FCSTD DOCUMENT  (FreeCAD 0.20R26155 (Git))
Label: 918-418K2022Y40004
License: All rights reserved
LicenseURL: http://en.wikipedia.org/wiki/All_rights_reserved
objects: Sketcher::SketchObject×4, PartDesign::Body×1
note: 5 computed .brp shape members not serialized (recipe doc carries the construction recipe); baked Part::Feature solids carry a one-line shape summary decoded from their .brp

FEATURE [Sketcher::SketchObject] Sketch  label="Edge_Cuts_0.15"
  FullyConstrained = false
  MapMode = 5
  Support = -> [XY_Plane]
  sketch-geometry (8):
    g0: ArcOfCircle CenterX=3.54 CenterY=0 CenterZ=0 NormalX=0 NormalY=0 NormalZ=1 AngleXU=0 Radius=0.29 StartAngle=1.5708 EndAngle=4.71239
    g1: ArcOfCircle CenterX=3.96 CenterY=0 CenterZ=0 NormalX=0 NormalY=0 NormalZ=1 AngleXU=0 Radius=0.29 StartAngle=4.71239 EndAngle=7.85398
    g2: LineSegment StartX=3.54 StartY=-0.29 StartZ=0 EndX=3.96 EndY=-0.29 EndZ=0
    g3: LineSegment StartX=3.96 StartY=0.29 StartZ=0 EndX=3.54 EndY=0.29 EndZ=0
    g4: Circle CenterX=-3.75 CenterY=0 CenterZ=0 NormalX=0 NormalY=0 NormalZ=1 AngleXU=0 Radius=0.33
    g5: LineSegment StartX=3.25 StartY=0.417733 StartZ=0 EndX=3.25 EndY=-0.637407 EndZ=0
    g6: LineSegment StartX=4.25 StartY=0.438122 StartZ=0 EndX=4.25 EndY=-0.525267 EndZ=0
    g7: LineSegment StartX=3.75 StartY=0.282998 StartZ=0 EndX=3.75 EndY=0 EndZ=0
  constraints (18):
    c: Tangent(g0,g2) = -1.5708
    c: Tangent(g2,g1) = -1.5708
    c: Tangent(g1,g3) = -1.5708
    c: Tangent(g3,g0) = -1.5708
    c: Equal(g0,g1)
    c: PointOnObject(g0,g-1)
    c: PointOnObject(g1,g-1)
    c: PointOnObject(g4,g-1)
    c: Radius(g4) = 0.33
    c: DistanceY(g1,g1) = 0.58
    c: Vertical(g5)
    c: Vertical(g6)
    c: Tangent(g6,g1)
    c: Tangent(g5,g0)
    c: Symmetric(g1,g0,g7)
    c: DistanceX(g5,g6) = 1
    c: DistanceX(g4,g7) = 7.5
    c: Symmetric(g4,g7,g-2)
FEATURE [Sketcher::SketchObject] Sketch001  label="Pads_TH_SMD1"
  ExternalGeometry = -> [Sketch]
  FullyConstrained = true
  MapMode = 5
  Support = -> [XY_Plane]
  sketch-geometry (12):
    g0: LineSegment StartX=-2.4 StartY=2.15 StartZ=0 EndX=2.4 EndY=2.15 EndZ=0
    g1: LineSegment StartX=2.4 StartY=2.15 StartZ=0 EndX=2.4 EndY=-2.15 EndZ=0
    g2: LineSegment StartX=2.4 StartY=-2.15 StartZ=0 EndX=-2.4 EndY=-2.15 EndZ=0
    g3: LineSegment StartX=-2.4 StartY=-2.15 StartZ=0 EndX=-2.4 EndY=2.15 EndZ=0
    g4: Circle CenterX=-2.4 CenterY=2.15 CenterZ=0 NormalX=0 NormalY=0 NormalZ=1 AngleXU=0 Radius=0.35
    g5: Circle CenterX=-2.4 CenterY=2.15 CenterZ=0 NormalX=0 NormalY=0 NormalZ=1 AngleXU=0 Radius=0.5
    g6: Circle CenterX=2.4 CenterY=2.15 CenterZ=0 NormalX=0 NormalY=0 NormalZ=1 AngleXU=0 Radius=0.35
    g7: Circle CenterX=2.4 CenterY=2.15 CenterZ=0 NormalX=0 NormalY=0 NormalZ=1 AngleXU=0 Radius=0.5
    g8: Circle CenterX=2.4 CenterY=-2.15 CenterZ=0 NormalX=0 NormalY=0 NormalZ=1 AngleXU=0 Radius=0.5
    g9: Circle CenterX=2.4 CenterY=-2.15 CenterZ=0 NormalX=0 NormalY=0 NormalZ=1 AngleXU=0 Radius=0.35
    g10: Circle CenterX=-2.4 CenterY=-2.15 CenterZ=0 NormalX=0 NormalY=0 NormalZ=1 AngleXU=0 Radius=0.5
    g11: Circle CenterX=-2.4 CenterY=-2.15 CenterZ=0 NormalX=0 NormalY=0 NormalZ=1 AngleXU=0 Radius=0.35
  constraints (27):
    c: Coincident(g0,g1)
    c: Coincident(g1,g2)
    c: Coincident(g2,g3)
    c: Coincident(g3,g0)
    c: Horizontal(g0)
    c: Horizontal(g2)
    c: Vertical(g3)
    c: Symmetric(g0,g1,g-1)
    c: DistanceY(g3,g3) = 4.3
    c: DistanceX(g-3,g2) = 1.35
    c: DistanceX(g-3,g1) = 6.15
    c: Coincident(g4,g0)
    c: Coincident(g5,g4)
    c: Coincident(g6,g0)
    c: Coincident(g7,g6)
    c: Coincident(g8,g1)
    c: Coincident(g9,g8)
    c: Coincident(g10,g2)
    c: Coincident(g11,g10)
    c: Equal(g9,g11)
    c: Equal(g11,g4)
    c: Equal(g4,g6)
    c: Radius(g9) = 0.35
    c: Equal(g8,g10)
    c: Equal(g10,g5)
    c: Equal(g5,g7)
    c: Radius(g8) = 0.5
FEATURE [Sketcher::SketchObject] Sketch002  label="Pads_TH_SMD"
  ExternalGeometry = -> [Sketch]
  FullyConstrained = true
  MapMode = 5
  Support = -> [XY_Plane]
  sketch-geometry (105):
    g0: LineSegment StartX=-2.9 StartY=1.25 StartZ=0 EndX=-2.6 EndY=1.25 EndZ=0
    g1: LineSegment StartX=-2.6 StartY=1.25 StartZ=0 EndX=-2.6 EndY=0.33 EndZ=0
    g2: LineSegment StartX=-2.6 StartY=0.33 StartZ=0 EndX=-2.9 EndY=0.33 EndZ=0
    g3: LineSegment StartX=-2.9 StartY=0.33 StartZ=0 EndX=-2.9 EndY=1.25 EndZ=0
    g4: LineSegment StartX=-2.9 StartY=0.33 StartZ=0 EndX=-3.75 EndY=0.33 EndZ=0
    g5: LineSegment StartX=-2.75 StartY=1.25 StartZ=0 EndX=-2.75 EndY=0.33 EndZ=0
    g6: LineSegment StartX=-2.9 StartY=-0.33 StartZ=0 EndX=-2.6 EndY=-0.33 EndZ=0
    g7: LineSegment StartX=-2.6 StartY=-0.33 StartZ=0 EndX=-2.6 EndY=-1.25 EndZ=0
    g8: LineSegment StartX=-2.6 StartY=-1.25 StartZ=0 EndX=-2.9 EndY=-1.25 EndZ=0
    g9: LineSegment StartX=-2.9 StartY=-1.25 StartZ=0 EndX=-2.9 EndY=-0.33 EndZ=0
    g10: LineSegment StartX=-2.75 StartY=-0.33 StartZ=0 EndX=-2.75 EndY=-1.25 EndZ=0
    g11: LineSegment StartX=-2.9 StartY=-0.33 StartZ=0 EndX=-3.75 EndY=-0.33 EndZ=0
    g12: LineSegment StartX=-2.75 StartY=1.25 StartZ=0 EndX=2.75 EndY=1.25 EndZ=0
    g13: LineSegment StartX=-2.75 StartY=-1.25 StartZ=0 EndX=2.75 EndY=-1.25 EndZ=0
    g14: LineSegment StartX=2.75 StartY=-1.25 StartZ=0 EndX=2.75 EndY=1.25 EndZ=0
    g15: LineSegment StartX=-2.6 StartY=0.33 StartZ=0 EndX=2.75 EndY=0.33 EndZ=0
    g16: LineSegment StartX=-2.6 StartY=-0.33 StartZ=0 EndX=2.75 EndY=-0.33 EndZ=0
    g17: LineSegment StartX=-2.4 StartY=1.25 StartZ=0 EndX=-2.1 EndY=1.25 EndZ=0
    g18: LineSegment StartX=-2.1 StartY=1.25 StartZ=0 EndX=-2.1 EndY=0.33 EndZ=0
    g19: LineSegment StartX=-2.1 StartY=0.33 StartZ=0 EndX=-2.4 EndY=0.33 EndZ=0
    g20: LineSegment StartX=-2.4 StartY=0.33 StartZ=0 EndX=-2.4 EndY=1.25 EndZ=0
    g21: LineSegment StartX=-1.9 StartY=1.25 StartZ=0 EndX=-1.6 EndY=1.25 EndZ=0
    g22: LineSegment StartX=-1.6 StartY=1.25 StartZ=0 EndX=-1.6 EndY=0.33 EndZ=0
    g23: LineSegment StartX=-1.6 StartY=0.33 StartZ=0 EndX=-1.9 EndY=0.33 EndZ=0
    g24: LineSegment StartX=-1.9 StartY=0.33 StartZ=0 EndX=-1.9 EndY=1.25 EndZ=0
    g25: LineSegment StartX=-1.4 StartY=1.25 StartZ=0 EndX=-1.1 EndY=1.25 EndZ=0
    g26: LineSegment StartX=-1.1 StartY=1.25 StartZ=0 EndX=-1.1 EndY=0.33 EndZ=0
    g27: LineSegment StartX=-1.1 StartY=0.33 StartZ=0 EndX=-1.4 EndY=0.33 EndZ=0
    g28: LineSegment StartX=-1.4 StartY=0.33 StartZ=0 EndX=-1.4 EndY=1.25 EndZ=0
    g29: LineSegment StartX=-0.9 StartY=1.25 StartZ=0 EndX=-0.6 EndY=1.25 EndZ=0
    g30: LineSegment StartX=-0.6 StartY=1.25 StartZ=0 EndX=-0.6 EndY=0.33 EndZ=0
    g31: LineSegment StartX=-0.6 StartY=0.33 StartZ=0 EndX=-0.9 EndY=0.33 EndZ=0
    g32: LineSegment StartX=-0.9 StartY=0.33 StartZ=0 EndX=-0.9 EndY=1.25 EndZ=0
    g33: LineSegment StartX=-0.4 StartY=1.25 StartZ=0 EndX=-0.1 EndY=1.25 EndZ=0
    g34: LineSegment StartX=-0.1 StartY=1.25 StartZ=0 EndX=-0.1 EndY=0.33 EndZ=0
    g35: LineSegment StartX=-0.1 StartY=0.33 StartZ=0 EndX=-0.4 EndY=0.33 EndZ=0
    g36: LineSegment StartX=-0.4 StartY=0.33 StartZ=0 EndX=-0.4 EndY=1.25 EndZ=0
    g37: LineSegment StartX=0.1 StartY=1.25 StartZ=0 EndX=0.4 EndY=1.25 EndZ=0
    g38: LineSegment StartX=0.4 StartY=1.25 StartZ=0 EndX=0.4 EndY=0.33 EndZ=0
    g39: LineSegment StartX=0.4 StartY=0.33 StartZ=0 EndX=0.1 EndY=0.33 EndZ=0
    g40: LineSegment StartX=0.1 StartY=0.33 StartZ=0 EndX=0.1 EndY=1.25 EndZ=0
    g41: LineSegment StartX=0.6 StartY=1.25 StartZ=0 EndX=0.9 EndY=1.25 EndZ=0
    g42: LineSegment StartX=0.9 StartY=1.25 StartZ=0 EndX=0.9 EndY=0.33 EndZ=0
    g43: LineSegment StartX=0.9 StartY=0.33 StartZ=0 EndX=0.6 EndY=0.33 EndZ=0
    g44: LineSegment StartX=0.6 StartY=0.33 StartZ=0 EndX=0.6 EndY=1.25 EndZ=0
    g45: LineSegment StartX=1.1 StartY=1.25 StartZ=0 EndX=1.4 EndY=1.25 EndZ=0
    g46: LineSegment StartX=1.4 StartY=1.25 StartZ=0 EndX=1.4 EndY=0.33 EndZ=0
    g47: LineSegment StartX=1.4 StartY=0.33 StartZ=0 EndX=1.1 EndY=0.33 EndZ=0
    g48: LineSegment StartX=1.1 StartY=0.33 StartZ=0 EndX=1.1 EndY=1.25 EndZ=0
    g49: LineSegment StartX=1.6 StartY=1.25 StartZ=0 EndX=1.9 EndY=1.25 EndZ=0
    g50: LineSegment StartX=1.9 StartY=1.25 StartZ=0 EndX=1.9 EndY=0.33 EndZ=0
    g51: LineSegment StartX=1.9 StartY=0.33 StartZ=0 EndX=1.6 EndY=0.33 EndZ=0
    g52: LineSegment StartX=1.6 StartY=0.33 StartZ=0 EndX=1.6 EndY=1.25 EndZ=0
    g53: LineSegment StartX=2.1 StartY=1.25 StartZ=0 EndX=2.4 EndY=1.25 EndZ=0
    g54: LineSegment StartX=2.4 StartY=1.25 StartZ=0 EndX=2.4 EndY=0.33 EndZ=0
    g55: LineSegment StartX=2.4 StartY=0.33 StartZ=0 EndX=2.1 EndY=0.33 EndZ=0
    g56: LineSegment StartX=2.1 StartY=0.33 StartZ=0 EndX=2.1 EndY=1.25 EndZ=0
    g57: LineSegment StartX=2.6 StartY=1.25 StartZ=0 EndX=2.9 EndY=1.25 EndZ=0
    g58: LineSegment StartX=2.9 StartY=1.25 StartZ=0 EndX=2.9 EndY=0.33 EndZ=0
    g59: LineSegment StartX=2.9 StartY=0.33 StartZ=0 EndX=2.6 EndY=0.33 EndZ=0
    g60: LineSegment StartX=2.6 StartY=0.33 StartZ=0 EndX=2.6 EndY=1.25 EndZ=0
    g61: LineSegment StartX=-2.4 StartY=-0.33 StartZ=0 EndX=-2.1 EndY=-0.33 EndZ=0
    g62: LineSegment StartX=-2.1 StartY=-0.33 StartZ=0 EndX=-2.1 EndY=-1.25 EndZ=0
    g63: LineSegment StartX=-2.1 StartY=-1.25 StartZ=0 EndX=-2.4 EndY=-1.25 EndZ=0
    g64: LineSegment StartX=-2.4 StartY=-1.25 StartZ=0 EndX=-2.4 EndY=-0.33 EndZ=0
    g65: LineSegment StartX=-1.9 StartY=-0.33 StartZ=0 EndX=-1.6 EndY=-0.33 EndZ=0
    g66: LineSegment StartX=-1.6 StartY=-0.33 StartZ=0 EndX=-1.6 EndY=-1.25 EndZ=0
    g67: LineSegment StartX=-1.6 StartY=-1.25 StartZ=0 EndX=-1.9 EndY=-1.25 EndZ=0
    g68: LineSegment StartX=-1.9 StartY=-1.25 StartZ=0 EndX=-1.9 EndY=-0.33 EndZ=0
    g69: LineSegment StartX=-1.4 StartY=-0.33 StartZ=0 EndX=-1.1 EndY=-0.33 EndZ=0
    g70: LineSegment StartX=-1.1 StartY=-0.33 StartZ=0 EndX=-1.1 EndY=-1.25 EndZ=0
    g71: LineSegment StartX=-1.1 StartY=-1.25 StartZ=0 EndX=-1.4 EndY=-1.25 EndZ=0
    g72: LineSegment StartX=-1.4 StartY=-1.25 StartZ=0 EndX=-1.4 EndY=-0.33 EndZ=0
    g73: LineSegment StartX=-0.9 StartY=-0.33 StartZ=0 EndX=-0.6 EndY=-0.33 EndZ=0
    g74: LineSegment StartX=-0.6 StartY=-0.33 StartZ=0 EndX=-0.6 EndY=-1.25 EndZ=0
    g75: LineSegment StartX=-0.6 StartY=-1.25 StartZ=0 EndX=-0.9 EndY=-1.25 EndZ=0
    g76: LineSegment StartX=-0.9 StartY=-1.25 StartZ=0 EndX=-0.9 EndY=-0.33 EndZ=0
    g77: LineSegment StartX=-0.4 StartY=-0.33 StartZ=0 EndX=-0.1 EndY=-0.33 EndZ=0
    g78: LineSegment StartX=-0.1 StartY=-0.33 StartZ=0 EndX=-0.1 EndY=-1.25 EndZ=0
    g79: LineSegment StartX=-0.1 StartY=-1.25 StartZ=0 EndX=-0.4 EndY=-1.25 EndZ=0
    g80: LineSegment StartX=-0.4 StartY=-1.25 StartZ=0 EndX=-0.4 EndY=-0.33 EndZ=0
    g81: LineSegment StartX=0.1 StartY=-0.33 StartZ=0 EndX=0.4 EndY=-0.33 EndZ=0
    g82: LineSegment StartX=0.4 StartY=-0.33 StartZ=0 EndX=0.4 EndY=-1.25 EndZ=0
    g83: LineSegment StartX=0.4 StartY=-1.25 StartZ=0 EndX=0.1 EndY=-1.25 EndZ=0
    g84: LineSegment StartX=0.1 StartY=-1.25 StartZ=0 EndX=0.1 EndY=-0.33 EndZ=0
    g85: LineSegment StartX=0.6 StartY=-0.33 StartZ=0 EndX=0.9 EndY=-0.33 EndZ=0
    g86: LineSegment StartX=0.9 StartY=-0.33 StartZ=0 EndX=0.9 EndY=-1.25 EndZ=0
    g87: LineSegment StartX=0.9 StartY=-1.25 StartZ=0 EndX=0.6 EndY=-1.25 EndZ=0
    g88: LineSegment StartX=0.6 StartY=-1.25 StartZ=0 EndX=0.6 EndY=-0.33 EndZ=0
    g89: LineSegment StartX=1.1 StartY=-0.33 StartZ=0 EndX=1.4 EndY=-0.33 EndZ=0
    g90: LineSegment StartX=1.4 StartY=-0.33 StartZ=0 EndX=1.4 EndY=-1.25 EndZ=0
    g91: LineSegment StartX=1.4 StartY=-1.25 StartZ=0 EndX=1.1 EndY=-1.25 EndZ=0
    g92: LineSegment StartX=1.1 StartY=-1.25 StartZ=0 EndX=1.1 EndY=-0.33 EndZ=0
    g93: LineSegment StartX=1.6 StartY=-0.33 StartZ=0 EndX=1.9 EndY=-0.33 EndZ=0
    g94: LineSegment StartX=1.9 StartY=-0.33 StartZ=0 EndX=1.9 EndY=-1.25 EndZ=0
    g95: LineSegment StartX=1.9 StartY=-1.25 StartZ=0 EndX=1.6 EndY=-1.25 EndZ=0
    g96: LineSegment StartX=1.6 StartY=-1.25 StartZ=0 EndX=1.6 EndY=-0.33 EndZ=0
    g97: LineSegment StartX=2.1 StartY=-0.33 StartZ=0 EndX=2.4 EndY=-0.33 EndZ=0
    g98: LineSegment StartX=2.4 StartY=-0.33 StartZ=0 EndX=2.4 EndY=-1.25 EndZ=0
    g99: LineSegment StartX=2.4 StartY=-1.25 StartZ=0 EndX=2.1 EndY=-1.25 EndZ=0
    g100: LineSegment StartX=2.1 StartY=-1.25 StartZ=0 EndX=2.1 EndY=-0.33 EndZ=0
    g101: LineSegment StartX=2.6 StartY=-1.25 StartZ=0 EndX=2.9 EndY=-1.25 EndZ=0
    g102: LineSegment StartX=2.9 StartY=-1.25 StartZ=0 EndX=2.9 EndY=-0.33 EndZ=0
    g103: LineSegment StartX=2.9 StartY=-0.33 StartZ=0 EndX=2.6 EndY=-0.33 EndZ=0
    g104: LineSegment StartX=2.6 StartY=-0.33 StartZ=0 EndX=2.6 EndY=-1.25 EndZ=0
  constraints (312):
    c: Coincident(g0,g1)
    c: Coincident(g1,g2)
    c: Coincident(g2,g3)
    c: Coincident(g3,g0)
    c: Horizontal(g0)
    c: Horizontal(g2)
    c: Vertical(g1)
    c: Vertical(g3)
    c: DistanceX(g0,g0) = 0.3
    c: Coincident(g4,g2)
    c: Horizontal(g4)
    c: Tangent(g4,g-3) = -1.5708
    c: PointOnObject(g5,g0)
    c: PointOnObject(g5,g2)
    c: Symmetric(g1,g2,g5)
    c: DistanceX(g-3,g5) = 1
    c: DistanceY(g-3,g5) = 1.25
    c: Coincident(g6,g7)
    c: Coincident(g7,g8)
    c: Coincident(g8,g9)
    c: Coincident(g9,g6)
    c: Horizontal(g6)
    c: Horizontal(g8)
    c: Vertical(g7)
    c: Vertical(g9)
    c: DistanceX(g8,g8) = 0.3
    c: PointOnObject(g10,g6)
    c: PointOnObject(g10,g8)
    c: Symmetric(g7,g8,g10)
    c: Coincident(g11,g6)
    c: Horizontal(g11)
    c: Tangent(g11,g-3) = 1.5708
    c: DistanceY(g8,g-3) = 1.25
    c: DistanceX(g-3,g10) = 1
    c: Coincident(g12,g5)
    c: Horizontal(g12)
    c: Coincident(g13,g10)
    c: Horizontal(g13)
    c: Coincident(g14,g13)
    c: Coincident(g14,g12)
    c: Vertical(g14)
    c: DistanceX(g-3,g12) = 6.5
    c: Coincident(g15,g1)
    c: PointOnObject(g15,g14)
    c: Horizontal(g15)
    c: Coincident(g16,g6)
    c: PointOnObject(g16,g14)
    c: Horizontal(g16)
    c: Coincident(g17,g18)
    c: Coincident(g18,g19)
    c: Coincident(g19,g20)
    c: Coincident(g20,g17)
    c: Horizontal(g17)
    c: Horizontal(g19)
    c: Vertical(g18)
    c: Vertical(g20)
    c: PointOnObject(g17,g12)
    c: PointOnObject(g18,g15)
    c: Coincident(g21,g22)
    c: Coincident(g22,g23)
    c: Coincident(g23,g24)
    c: Coincident(g24,g21)
    c: Horizontal(g21)
    c: Horizontal(g23)
    c: Vertical(g22)
    c: Vertical(g24)
    c: PointOnObject(g21,g12)
    c: PointOnObject(g22,g15)
    c: Coincident(g25,g26)
    c: Coincident(g26,g27)
    c: Coincident(g27,g28)
    c: Coincident(g28,g25)
    c: Horizontal(g25)
    c: Horizontal(g27)
    c: Vertical(g26)
    c: Vertical(g28)
    c: PointOnObject(g25,g12)
    c: PointOnObject(g26,g15)
    c: Coincident(g29,g30)
    c: Coincident(g30,g31)
    c: Coincident(g31,g32)
    c: Coincident(g32,g29)
    c: Horizontal(g29)
    c: Horizontal(g31)
    c: Vertical(g30)
    c: Vertical(g32)
    c: PointOnObject(g29,g12)
    c: PointOnObject(g30,g15)
    c: Coincident(g33,g34)
    c: Coincident(g34,g35)
    c: Coincident(g35,g36)
    c: Coincident(g36,g33)
    c: Horizontal(g33)
    c: Horizontal(g35)
    c: Vertical(g34)
    c: Vertical(g36)
    c: PointOnObject(g33,g12)
    c: PointOnObject(g34,g15)
    c: Coincident(g37,g38)
    c: Coincident(g38,g39)
    c: Coincident(g39,g40)
    c: Coincident(g40,g37)
    c: Horizontal(g37)
    c: Horizontal(g39)
    c: Vertical(g38)
    c: Vertical(g40)
    c: PointOnObject(g37,g12)
    c: PointOnObject(g38,g15)
    c: Coincident(g41,g42)
    c: Coincident(g42,g43)
    c: Coincident(g43,g44)
    c: Coincident(g44,g41)
    c: Horizontal(g41)
    c: Horizontal(g43)
    c: Vertical(g42)
    c: Vertical(g44)
    c: PointOnObject(g41,g12)
    c: PointOnObject(g42,g15)
    c: Coincident(g45,g46)
    c: Coincident(g46,g47)
    c: Coincident(g47,g48)
    c: Coincident(g48,g45)
    c: Horizontal(g45)
    c: Horizontal(g47)
    c: Vertical(g46)
    c: Vertical(g48)
    c: PointOnObject(g45,g12)
    c: PointOnObject(g46,g15)
    c: Coincident(g49,g50)
    c: Coincident(g50,g51)
    c: Coincident(g51,g52)
    c: Coincident(g52,g49)
    c: Horizontal(g49)
    c: Horizontal(g51)
    c: Vertical(g50)
    c: Vertical(g52)
    c: PointOnObject(g49,g12)
    c: PointOnObject(g50,g15)
    c: Equal(g17,g21)
    c: Equal(g21,g25)
    c: Equal(g25,g29)
    c: Equal(g29,g33)
    c: Equal(g33,g37)
    c: Equal(g37,g41)
    c: Equal(g41,g45)
    c: Equal(g45,g49)
    c: Equal(g49,g0)
    c: DistanceX(g1,g19) = 0.2
    c: DistanceX(g18,g23) = 0.2
    c: DistanceX(g22,g27) = 0.2
    c: DistanceX(g26,g31) = 0.2
    c: DistanceX(g30,g35) = 0.2
    c: DistanceX(g34,g39) = 0.2
    c: DistanceX(g38,g43) = 0.2
    c: DistanceX(g42,g47) = 0.2
    c: DistanceX(g46,g51) = 0.2
    c: Coincident(g53,g54)
    c: Coincident(g54,g55)
    c: Coincident(g55,g56)
    c: Coincident(g56,g53)
    c: Horizontal(g53)
    c: Horizontal(g55)
    c: Vertical(g54)
    c: Vertical(g56)
    c: PointOnObject(g53,g12)
    c: PointOnObject(g54,g15)
    c: Coincident(g57,g58)
    c: Coincident(g58,g59)
    c: Coincident(g59,g60)
    c: Coincident(g60,g57)
    c: Horizontal(g57)
    c: Horizontal(g59)
    c: Vertical(g58)
    c: Vertical(g60)
    c: PointOnObject(g57,g12)
    c: PointOnObject(g59,g15)
    c: DistanceX(g50,g55) = 0.2
    c: Equal(g53,g57)
    c: Equal(g57,g49)
    c: DistanceX(g54,g59) = 0.2
    c: Coincident(g61,g62)
    c: Coincident(g62,g63)
    c: Coincident(g63,g64)
    c: Coincident(g64,g61)
    c: Horizontal(g61)
    c: Horizontal(g63)
    c: Vertical(g62)
    c: Vertical(g64)
    c: PointOnObject(g61,g16)
    c: Coincident(g65,g66)
    c: Coincident(g66,g67)
    c: Coincident(g67,g68)
    c: Coincident(g68,g65)
    c: Horizontal(g65)
    c: Horizontal(g67)
    c: Vertical(g66)
    c: Vertical(g68)
    c: PointOnObject(g65,g16)
    c: PointOnObject(g66,g13)
    c: Coincident(g69,g70)
    c: Coincident(g70,g71)
    c: Coincident(g71,g72)
    c: Coincident(g72,g69)
    c: Horizontal(g69)
    c: Horizontal(g71)
    c: Vertical(g70)
    c: Vertical(g72)
    c: PointOnObject(g69,g16)
    c: PointOnObject(g70,g13)
    c: Coincident(g73,g74)
    c: Coincident(g74,g75)
    c: Coincident(g75,g76)
    c: Coincident(g76,g73)
    c: Horizontal(g73)
    c: Horizontal(g75)
    c: Vertical(g74)
    c: Vertical(g76)
    c: PointOnObject(g73,g16)
    c: PointOnObject(g74,g13)
    c: Coincident(g77,g78)
    c: Coincident(g78,g79)
    c: Coincident(g79,g80)
    c: Coincident(g80,g77)
    c: Horizontal(g77)
    c: Horizontal(g79)
    c: Vertical(g78)
    c: Vertical(g80)
    c: PointOnObject(g77,g16)
    c: PointOnObject(g78,g13)
    c: Coincident(g81,g82)
    c: Coincident(g82,g83)
    c: Coincident(g83,g84)
    c: Coincident(g84,g81)
    c: Horizontal(g81)
    c: Horizontal(g83)
    c: Vertical(g82)
    c: Vertical(g84)
    c: PointOnObject(g81,g16)
    c: PointOnObject(g82,g13)
    c: Coincident(g85,g86)
    c: Coincident(g86,g87)
    c: Coincident(g87,g88)
    c: Coincident(g88,g85)
    c: Horizontal(g85)
    c: Horizontal(g87)
    c: Vertical(g86)
    c: Vertical(g88)
    c: PointOnObject(g85,g16)
    c: PointOnObject(g86,g13)
    c: Coincident(g89,g90)
    c: Coincident(g90,g91)
    c: Coincident(g91,g92)
    c: Coincident(g92,g89)
    c: Horizontal(g89)
    c: Horizontal(g91)
    c: Vertical(g90)
    c: Vertical(g92)
    c: PointOnObject(g89,g16)
    c: PointOnObject(g90,g13)
    c: Coincident(g93,g94)
    c: Coincident(g94,g95)
    c: Coincident(g95,g96)
    c: Coincident(g96,g93)
    c: Horizontal(g93)
    c: Horizontal(g95)
    c: Vertical(g94)
    c: Vertical(g96)
    c: PointOnObject(g93,g16)
    c: PointOnObject(g94,g13)
    c: Coincident(g97,g98)
    c: Coincident(g98,g99)
    c: Coincident(g99,g100)
    c: Coincident(g100,g97)
    c: Horizontal(g97)
    c: Horizontal(g99)
    c: Vertical(g98)
    c: Vertical(g100)
    c: PointOnObject(g97,g16)
    c: PointOnObject(g98,g13)
    c: Coincident(g101,g102)
    c: Coincident(g102,g103)
    c: Coincident(g103,g104)
    c: Coincident(g104,g101)
    c: Horizontal(g101)
    c: Horizontal(g103)
    c: Vertical(g102)
    c: Vertical(g104)
    c: PointOnObject(g101,g13)
    c: Equal(g61,g65)
    c: Equal(g65,g69)
    c: Equal(g69,g73)
    c: Equal(g73,g77)
    c: Equal(g77,g81)
    c: Equal(g81,g85)
    c: Equal(g85,g89)
    c: Equal(g89,g93)
    c: Equal(g93,g97)
    c: Equal(g97,g103)
    c: Equal(g103,g6)
    c: PointOnObject(g103,g16)
    c: PointOnObject(g63,g13)
    c: DistanceX(g7,g63) = 0.2
    c: DistanceX(g62,g67) = 0.2
    c: DistanceX(g66,g71) = 0.2
    c: DistanceX(g70,g75) = 0.2
    c: DistanceX(g74,g79) = 0.2
    c: DistanceX(g78,g83) = 0.2
    c: DistanceX(g82,g87) = 0.2
    c: DistanceX(g86,g91) = 0.2
    c: DistanceX(g90,g95) = 0.2
    c: DistanceX(g94,g99) = 0.2
    c: DistanceX(g98,g101) = 0.2
FEATURE [Sketcher::SketchObject] Sketch003  label="F_Fab_0.1"
  FullyConstrained = true
  MapMode = 5
  Support = -> [XY_Plane]
  sketch-geometry (4):
    g0: LineSegment StartX=-5 StartY=2.3 StartZ=0 EndX=5 EndY=2.3 EndZ=0
    g1: LineSegment StartX=5 StartY=2.3 StartZ=0 EndX=5 EndY=-2.3 EndZ=0
    g2: LineSegment StartX=5 StartY=-2.3 StartZ=0 EndX=-5 EndY=-2.3 EndZ=0
    g3: LineSegment StartX=-5 StartY=-2.3 StartZ=0 EndX=-5 EndY=2.3 EndZ=0
  constraints (10):
    c: Coincident(g0,g1)
    c: Coincident(g1,g2)
    c: Coincident(g2,g3)
    c: Coincident(g3,g0)
    c: Horizontal(g2)
    c: Vertical(g3)
    c: Symmetric(g0,g0,g-2)
    c: Symmetric(g0,g1,g-1)
    c: DistanceY(g1,g1) = 4.6
    c: DistanceX(g0,g0) = 10
FEATURE [PartDesign::Body] Body
  Group = -> [Sketch,Sketch001,Sketch002,Sketch003]
  Origin = -> Origin
